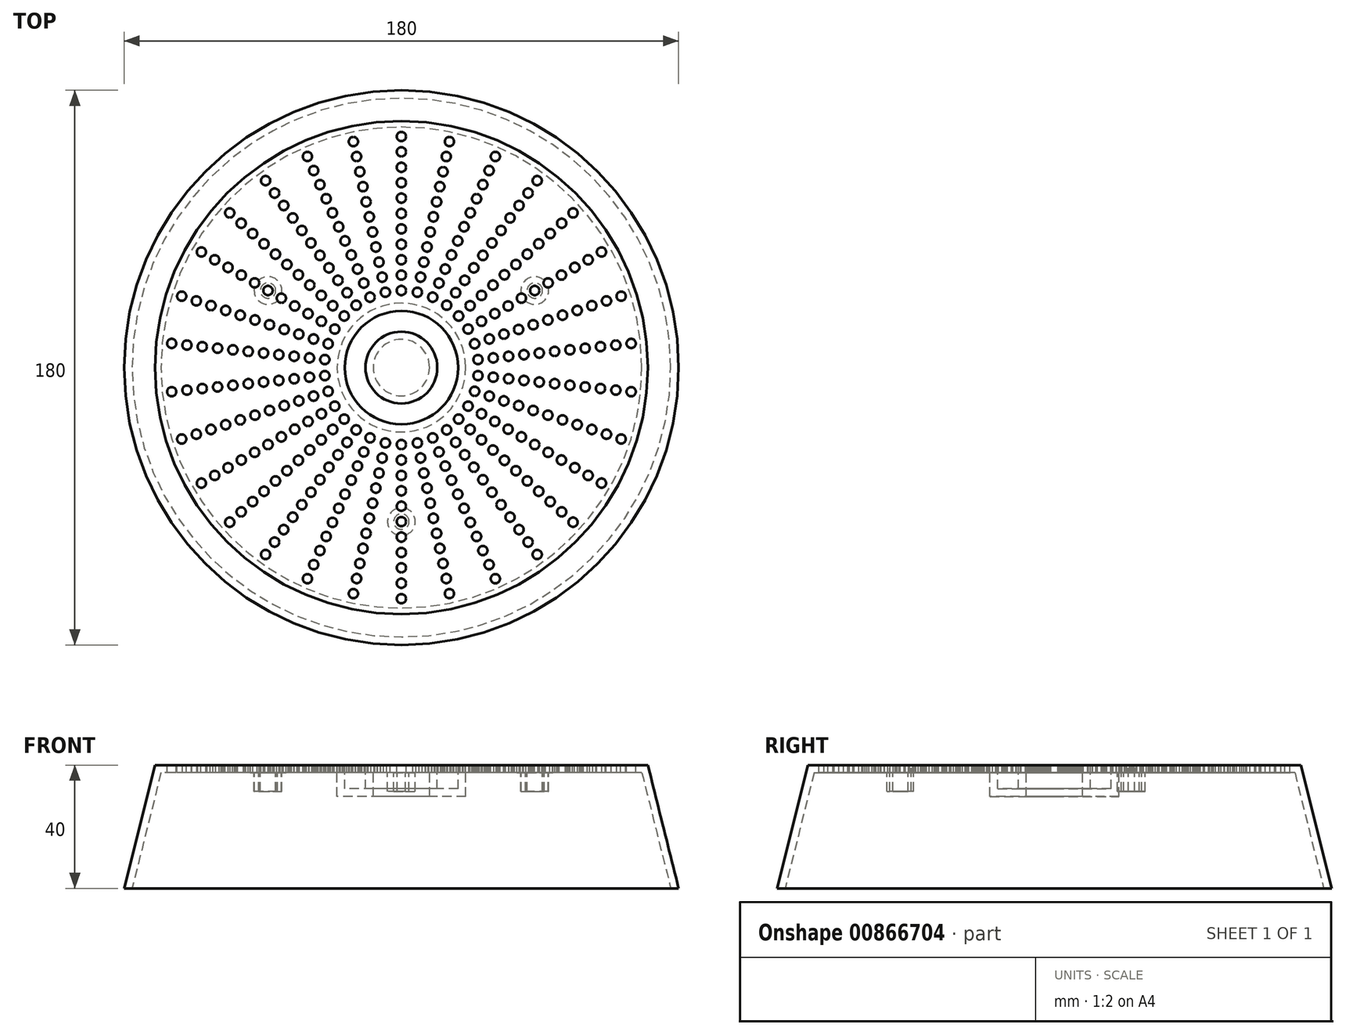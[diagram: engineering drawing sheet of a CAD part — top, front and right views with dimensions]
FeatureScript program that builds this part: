
annotation { "Feature Type Name" : "Feature", "Feature Type Description" : "" }
export const myFeature = defineFeature(function(context is Context, id is Id, definition is map)
    precondition{}
    {
        {
            var Q0;
            Q0=qCreatedBy(makeId("Top.planeOp"),FACE);
            var sketch = newSketch(context, id + "F0", { "sketchPlane" : qUnion([Q0])});
            skCircle(sketch, "E0", {"center": v(0, 0) * mm, "radius": 90 * mm});
            skSolve(sketch);
        }
        {
            var Q0;
            Q0=makeQuery(id+"F0.imprint","IMPRINT",FACE,{"disambiguationData":[TD([[makeQuery(id+"F0.imprint","IMPRINT",EDGE,{"derivedFrom":sQuery(id+"F0.wireOp",EDGE,"E0")}),1.0]])]});
            var Q1;
            Q1=makeQuery(id+"F0.imprint","IMPRINT",FACE,{"disambiguationData":[TD([[makeQuery(id+"F0.imprint","IMPRINT",EDGE,{"derivedFrom":sQuery(id+"F0.wireOp",EDGE,"Ynb0LsxG-EY0P-LQyA-zYZy-US9xmQLmgcTj")}),1.0]])]});
            var Q2;
            Q2=makeQuery(id+"F0.imprint","IMPRINT",FACE,{"disambiguationData":[TD([[makeQuery(id+"F0.imprint","IMPRINT",EDGE,{"derivedFrom":sQuery(id+"F0.wireOp",EDGE,"hYWYR66z-NgrN-YKXc-1CsE-6s0Bsp8cXAIZ")}),1.0]])]});
            extrude(context, id + "F1", {"entities" : qUnion([Q0, Q1, Q2]), "depth" : 40 * mm, "offsetDistance" : 25 * mm});
        }
        {
            var Q0;
            Q0=makeQuery(id+"F1.opExtrude","CAP_FACE",FACE,{"disambiguationData":[OSD([sQuery(id+"F0.wireOp",EDGE,"E0")])],"isStart":false});
            var sketch = newSketch(context, id + "F2", { "sketchPlane" : qUnion([Q0])});
            skCircle(sketch, "E1", {"center": v(0, 0) * mm, "radius": 18.4 * mm});
            skCircle(sketch, "E2", {"center": v(0, 0) * mm, "radius": 11.65 * mm});
            skSolve(sketch);
        }
        {
            var Q0;
            Q0=makeQuery(id+"F2.imprint","IMPRINT",FACE,{"disambiguationData":[TD([[makeQuery(id+"F2.imprint","IMPRINT",EDGE,{"derivedFrom":sQuery(id+"F2.wireOp",EDGE,"E1")}),1.0]])]});
            extrude(context, id + "F3", {"entities" : qUnion([Q0]), "operationType" : NewBodyOperationType.REMOVE, "oppositeDirection" : true, "depth" : 7.7 * mm, "offsetDistance" : 25 * mm});
        }
        {
            var Q0;
            Q0=makeQuery(id+"F1.opExtrude","CAP_EDGE",EDGE,{"disambiguationData":[OSD([sQuery(id+"F0.wireOp",EDGE,"E0")])],"isStart":false});
            chamfer(context, id + "F4", {"entities" : qUnion([Q0]), "chamferType" : ChamferType.TWO_OFFSETS, "width1" : 10 * mm, "oppositeDirection" : false, "width2" : 40 * mm});
        }
        {
            var Q0;
            Q0=makeQuery(id+"F1.opExtrude","CAP_FACE",FACE,{"disambiguationData":[OSD([sQuery(id+"F0.wireOp",EDGE,"E0")])],"isStart":true});
            shell(context, id + "F5", {"entities" : qUnion([Q0]), "thickness" : 2.5 * mm});
        }
        {
            var Q0;
            {var subQ0=sQuery(id+"F0.wireOp",EDGE,"E0");Q0=makeQuery(id+"F5.opShell","OFFSET_FACE",FACE,{"disambiguationData":[OSD([subQ0]),TDD([makeQuery(id+"F3.boolean.opBoolean","SPLIT",FACE,{"disambiguationData":[TD([makeQuery(id+"F1.opExtrude","SWEPT_FACE",FACE,{"disambiguationData":[OSD([subQ0])]})])],"derivedFrom":makeQuery(id+"F1.opExtrude","CAP_FACE",FACE,{"disambiguationData":[OSD([subQ0])],"isStart":false})})])]});}
            var sketch = newSketch(context, id + "F6", { "sketchPlane" : qUnion([Q0])});
            skCircle(sketch, "E3", {"center": v(0, 50) * mm, "radius": 4.5 * mm});
            skCircle(sketch, "E4", {"center": v(0, 50) * mm, "radius": 2.5 * mm});
            skCircle(sketch, "E5.1.0", {"center": v(-43.3, -25) * mm, "radius": 2.5 * mm});
            skCircle(sketch, "E5.1.1", {"center": v(-43.3, -25) * mm, "radius": 4.5 * mm});
            skCircle(sketch, "E5.2.0", {"center": v(43.3, -25) * mm, "radius": 2.5 * mm});
            skCircle(sketch, "E5.2.1", {"center": v(43.3, -25) * mm, "radius": 4.5 * mm});
            skPoint(sketch, "E5.center", {"position": v(0, 0) * mm});
            skSolve(sketch);
        }
        {
            var Q0;
            Q0=makeQuery(id+"F6.imprint","IMPRINT",FACE,{"disambiguationData":[TD([[makeQuery(id+"F6.imprint","IMPRINT",EDGE,{"derivedFrom":sQuery(id+"F6.wireOp",EDGE,"E3")}),1.0]])]});
            var Q1;
            Q1=makeQuery(id+"F6.imprint","IMPRINT",FACE,{"disambiguationData":[TD([[makeQuery(id+"F6.imprint","IMPRINT",EDGE,{"derivedFrom":sQuery(id+"F6.wireOp",EDGE,"E5.2.0")}),-1.0]])]});
            var Q2;
            Q2=makeQuery(id+"F6.imprint","IMPRINT",FACE,{"disambiguationData":[TD([[makeQuery(id+"F6.imprint","IMPRINT",EDGE,{"derivedFrom":sQuery(id+"F6.wireOp",EDGE,"E5.1.0")}),-1.0]])]});
            extrude(context, id + "F7", {"entities" : qUnion([Q0, Q1, Q2]), "operationType" : NewBodyOperationType.ADD, "depth" : 6 * mm, "offsetDistance" : 25 * mm});
        }
        {
            var Q0;
            {var subQ0=sQuery(id+"F0.wireOp",EDGE,"E0");Q0=makeQuery(id+"F3.boolean.opBoolean","SPLIT",FACE,{"disambiguationData":[TD([makeQuery(id+"F1.opExtrude","SWEPT_FACE",FACE,{"disambiguationData":[OSD([subQ0])]})])],"derivedFrom":makeQuery(id+"F1.opExtrude","CAP_FACE",FACE,{"disambiguationData":[OSD([subQ0])],"isStart":false})});}
            var sketch = newSketch(context, id + "F8", { "sketchPlane" : qUnion([Q0])});
            skCircle(sketch, "E6", {"center": v(0, 25) * mm, "radius": 1.5 * mm});
            skCircle(sketch, "E7.0.1.0", {"center": v(0, 30) * mm, "radius": 1.5 * mm});
            skCircle(sketch, "E7.0.2.0", {"center": v(0, 35) * mm, "radius": 1.5 * mm});
            skCircle(sketch, "E7.0.3.0", {"center": v(0, 40) * mm, "radius": 1.5 * mm});
            skCircle(sketch, "E7.0.4.0", {"center": v(0, 45) * mm, "radius": 1.5 * mm});
            skCircle(sketch, "E7.0.5.0", {"center": v(0, 50) * mm, "radius": 1.5 * mm});
            skCircle(sketch, "E7.0.6.0", {"center": v(0, 55) * mm, "radius": 1.5 * mm});
            skCircle(sketch, "E7.0.7.0", {"center": v(0, 60) * mm, "radius": 1.5 * mm});
            skCircle(sketch, "E7.0.8.0", {"center": v(0, 65) * mm, "radius": 1.5 * mm});
            skCircle(sketch, "E7.0.9.0", {"center": v(0, 70) * mm, "radius": 1.5 * mm});
            skCircle(sketch, "E7.0.10.0", {"center": v(0, 75) * mm, "radius": 1.5 * mm});
            skLineSegment(sketch, "E7.direction1", {"start": v(0, 25) * mm, "end": v(6.9, 25) * mm, "construction": true});
            skLineSegment(sketch, "E7.direction2", {"start": v(0, 25) * mm, "end": v(0, 30) * mm, "construction": true});
            skCircle(sketch, "E8.1.0", {"center": v(-10.4, 48.9) * mm, "radius": 1.5 * mm});
            skCircle(sketch, "E8.1.1", {"center": v(-5.2, 24.45) * mm, "radius": 1.5 * mm});
            skCircle(sketch, "E8.1.2", {"center": v(-6.24, 29.34) * mm, "radius": 1.5 * mm});
            skCircle(sketch, "E8.1.3", {"center": v(-7.28, 34.24) * mm, "radius": 1.5 * mm});
            skCircle(sketch, "E8.1.4", {"center": v(-8.32, 39.13) * mm, "radius": 1.5 * mm});
            skCircle(sketch, "E8.1.5", {"center": v(-9.36, 44.02) * mm, "radius": 1.5 * mm});
            skCircle(sketch, "E8.1.6", {"center": v(-11.44, 53.8) * mm, "radius": 1.5 * mm});
            skCircle(sketch, "E8.1.7", {"center": v(-12.47, 58.69) * mm, "radius": 1.5 * mm});
            skCircle(sketch, "E8.1.8", {"center": v(-13.51, 63.58) * mm, "radius": 1.5 * mm});
            skCircle(sketch, "E8.1.9", {"center": v(-14.55, 68.47) * mm, "radius": 1.5 * mm});
            skCircle(sketch, "E8.1.10", {"center": v(-15.6, 73.36) * mm, "radius": 1.5 * mm});
            skCircle(sketch, "E8.2.0", {"center": v(-20.34, 45.68) * mm, "radius": 1.5 * mm});
            skCircle(sketch, "E8.2.1", {"center": v(-10.17, 22.84) * mm, "radius": 1.5 * mm});
            skCircle(sketch, "E8.2.2", {"center": v(-12.2, 27.4) * mm, "radius": 1.5 * mm});
            skCircle(sketch, "E8.2.3", {"center": v(-14.24, 31.97) * mm, "radius": 1.5 * mm});
            skCircle(sketch, "E8.2.4", {"center": v(-16.27, 36.54) * mm, "radius": 1.5 * mm});
            skCircle(sketch, "E8.2.5", {"center": v(-18.3, 41.1) * mm, "radius": 1.5 * mm});
            skCircle(sketch, "E8.2.6", {"center": v(-22.37, 50.25) * mm, "radius": 1.5 * mm});
            skCircle(sketch, "E8.2.7", {"center": v(-24.4, 54.81) * mm, "radius": 1.5 * mm});
            skCircle(sketch, "E8.2.8", {"center": v(-26.44, 59.38) * mm, "radius": 1.5 * mm});
            skCircle(sketch, "E8.2.9", {"center": v(-28.47, 63.95) * mm, "radius": 1.5 * mm});
            skCircle(sketch, "E8.2.10", {"center": v(-30.5, 68.52) * mm, "radius": 1.5 * mm});
            skCircle(sketch, "E8.3.0", {"center": v(-29.39, 40.45) * mm, "radius": 1.5 * mm});
            skCircle(sketch, "E8.3.1", {"center": v(-14.7, 20.23) * mm, "radius": 1.5 * mm});
            skCircle(sketch, "E8.3.2", {"center": v(-17.63, 24.27) * mm, "radius": 1.5 * mm});
            skCircle(sketch, "E8.3.3", {"center": v(-20.57, 28.32) * mm, "radius": 1.5 * mm});
            skCircle(sketch, "E8.3.4", {"center": v(-23.51, 32.36) * mm, "radius": 1.5 * mm});
            skCircle(sketch, "E8.3.5", {"center": v(-26.45, 36.4) * mm, "radius": 1.5 * mm});
            skCircle(sketch, "E8.3.6", {"center": v(-32.33, 44.5) * mm, "radius": 1.5 * mm});
            skCircle(sketch, "E8.3.7", {"center": v(-35.27, 48.54) * mm, "radius": 1.5 * mm});
            skCircle(sketch, "E8.3.8", {"center": v(-38.2, 52.59) * mm, "radius": 1.5 * mm});
            skCircle(sketch, "E8.3.9", {"center": v(-41.14, 56.63) * mm, "radius": 1.5 * mm});
            skCircle(sketch, "E8.3.10", {"center": v(-44.08, 60.68) * mm, "radius": 1.5 * mm});
            skCircle(sketch, "E8.4.0", {"center": v(-37.16, 33.46) * mm, "radius": 1.5 * mm});
            skCircle(sketch, "E8.4.1", {"center": v(-18.58, 16.73) * mm, "radius": 1.5 * mm});
            skCircle(sketch, "E8.4.2", {"center": v(-22.3, 20.07) * mm, "radius": 1.5 * mm});
            skCircle(sketch, "E8.4.3", {"center": v(-26.01, 23.42) * mm, "radius": 1.5 * mm});
            skCircle(sketch, "E8.4.4", {"center": v(-29.73, 26.77) * mm, "radius": 1.5 * mm});
            skCircle(sketch, "E8.4.5", {"center": v(-33.44, 30.11) * mm, "radius": 1.5 * mm});
            skCircle(sketch, "E8.4.6", {"center": v(-40.87, 36.8) * mm, "radius": 1.5 * mm});
            skCircle(sketch, "E8.4.7", {"center": v(-44.59, 40.15) * mm, "radius": 1.5 * mm});
            skCircle(sketch, "E8.4.8", {"center": v(-48.3, 43.5) * mm, "radius": 1.5 * mm});
            skCircle(sketch, "E8.4.9", {"center": v(-52.02, 46.84) * mm, "radius": 1.5 * mm});
            skCircle(sketch, "E8.4.10", {"center": v(-55.74, 50.18) * mm, "radius": 1.5 * mm});
            skCircle(sketch, "E8.5.0", {"center": v(-43.3, 25) * mm, "radius": 1.5 * mm});
            skCircle(sketch, "E8.5.1", {"center": v(-21.65, 12.5) * mm, "radius": 1.5 * mm});
            skCircle(sketch, "E8.5.2", {"center": v(-25.98, 15) * mm, "radius": 1.5 * mm});
            skCircle(sketch, "E8.5.3", {"center": v(-30.31, 17.5) * mm, "radius": 1.5 * mm});
            skCircle(sketch, "E8.5.4", {"center": v(-34.64, 20) * mm, "radius": 1.5 * mm});
            skCircle(sketch, "E8.5.5", {"center": v(-38.97, 22.5) * mm, "radius": 1.5 * mm});
            skCircle(sketch, "E8.5.6", {"center": v(-47.63, 27.5) * mm, "radius": 1.5 * mm});
            skCircle(sketch, "E8.5.7", {"center": v(-51.96, 30) * mm, "radius": 1.5 * mm});
            skCircle(sketch, "E8.5.8", {"center": v(-56.3, 32.5) * mm, "radius": 1.5 * mm});
            skCircle(sketch, "E8.5.9", {"center": v(-60.62, 35) * mm, "radius": 1.5 * mm});
            skCircle(sketch, "E8.5.10", {"center": v(-64.95, 37.5) * mm, "radius": 1.5 * mm});
            skCircle(sketch, "E8.6.0", {"center": v(-47.55, 15.45) * mm, "radius": 1.5 * mm});
            skCircle(sketch, "E8.6.1", {"center": v(-23.78, 7.73) * mm, "radius": 1.5 * mm});
            skCircle(sketch, "E8.6.2", {"center": v(-28.53, 9.27) * mm, "radius": 1.5 * mm});
            skCircle(sketch, "E8.6.3", {"center": v(-33.29, 10.82) * mm, "radius": 1.5 * mm});
            skCircle(sketch, "E8.6.4", {"center": v(-38.04, 12.36) * mm, "radius": 1.5 * mm});
            skCircle(sketch, "E8.6.5", {"center": v(-42.8, 13.9) * mm, "radius": 1.5 * mm});
            skCircle(sketch, "E8.6.6", {"center": v(-52.3, 17) * mm, "radius": 1.5 * mm});
            skCircle(sketch, "E8.6.7", {"center": v(-57.06, 18.54) * mm, "radius": 1.5 * mm});
            skCircle(sketch, "E8.6.8", {"center": v(-61.82, 20.09) * mm, "radius": 1.5 * mm});
            skCircle(sketch, "E8.6.9", {"center": v(-66.57, 21.63) * mm, "radius": 1.5 * mm});
            skCircle(sketch, "E8.6.10", {"center": v(-71.33, 23.18) * mm, "radius": 1.5 * mm});
            skCircle(sketch, "E8.7.0", {"center": v(-49.73, 5.23) * mm, "radius": 1.5 * mm});
            skCircle(sketch, "E8.7.1", {"center": v(-24.86, 2.61) * mm, "radius": 1.5 * mm});
            skCircle(sketch, "E8.7.2", {"center": v(-29.84, 3.14) * mm, "radius": 1.5 * mm});
            skCircle(sketch, "E8.7.3", {"center": v(-34.8, 3.66) * mm, "radius": 1.5 * mm});
            skCircle(sketch, "E8.7.4", {"center": v(-39.78, 4.18) * mm, "radius": 1.5 * mm});
            skCircle(sketch, "E8.7.5", {"center": v(-44.75, 4.7) * mm, "radius": 1.5 * mm});
            skCircle(sketch, "E8.7.6", {"center": v(-54.7, 5.75) * mm, "radius": 1.5 * mm});
            skCircle(sketch, "E8.7.7", {"center": v(-59.67, 6.27) * mm, "radius": 1.5 * mm});
            skCircle(sketch, "E8.7.8", {"center": v(-64.64, 6.8) * mm, "radius": 1.5 * mm});
            skCircle(sketch, "E8.7.9", {"center": v(-69.62, 7.32) * mm, "radius": 1.5 * mm});
            skCircle(sketch, "E8.7.10", {"center": v(-74.59, 7.84) * mm, "radius": 1.5 * mm});
            skCircle(sketch, "E8.8.0", {"center": v(-49.73, -5.23) * mm, "radius": 1.5 * mm});
            skCircle(sketch, "E8.8.1", {"center": v(-24.86, -2.61) * mm, "radius": 1.5 * mm});
            skCircle(sketch, "E8.8.2", {"center": v(-29.84, -3.14) * mm, "radius": 1.5 * mm});
            skCircle(sketch, "E8.8.3", {"center": v(-34.8, -3.66) * mm, "radius": 1.5 * mm});
            skCircle(sketch, "E8.8.4", {"center": v(-39.78, -4.18) * mm, "radius": 1.5 * mm});
            skCircle(sketch, "E8.8.5", {"center": v(-44.75, -4.7) * mm, "radius": 1.5 * mm});
            skCircle(sketch, "E8.8.6", {"center": v(-54.7, -5.75) * mm, "radius": 1.5 * mm});
            skCircle(sketch, "E8.8.7", {"center": v(-59.67, -6.27) * mm, "radius": 1.5 * mm});
            skCircle(sketch, "E8.8.8", {"center": v(-64.64, -6.8) * mm, "radius": 1.5 * mm});
            skCircle(sketch, "E8.8.9", {"center": v(-69.62, -7.32) * mm, "radius": 1.5 * mm});
            skCircle(sketch, "E8.8.10", {"center": v(-74.59, -7.84) * mm, "radius": 1.5 * mm});
            skCircle(sketch, "E8.9.0", {"center": v(-47.55, -15.45) * mm, "radius": 1.5 * mm});
            skCircle(sketch, "E8.9.1", {"center": v(-23.78, -7.73) * mm, "radius": 1.5 * mm});
            skCircle(sketch, "E8.9.2", {"center": v(-28.53, -9.27) * mm, "radius": 1.5 * mm});
            skCircle(sketch, "E8.9.3", {"center": v(-33.29, -10.82) * mm, "radius": 1.5 * mm});
            skCircle(sketch, "E8.9.4", {"center": v(-38.04, -12.36) * mm, "radius": 1.5 * mm});
            skCircle(sketch, "E8.9.5", {"center": v(-42.8, -13.9) * mm, "radius": 1.5 * mm});
            skCircle(sketch, "E8.9.6", {"center": v(-52.3, -17) * mm, "radius": 1.5 * mm});
            skCircle(sketch, "E8.9.7", {"center": v(-57.06, -18.54) * mm, "radius": 1.5 * mm});
            skCircle(sketch, "E8.9.8", {"center": v(-61.82, -20.09) * mm, "radius": 1.5 * mm});
            skCircle(sketch, "E8.9.9", {"center": v(-66.57, -21.63) * mm, "radius": 1.5 * mm});
            skCircle(sketch, "E8.9.10", {"center": v(-71.33, -23.18) * mm, "radius": 1.5 * mm});
            skCircle(sketch, "E8.10.0", {"center": v(-43.3, -25) * mm, "radius": 1.5 * mm});
            skCircle(sketch, "E8.10.1", {"center": v(-21.65, -12.5) * mm, "radius": 1.5 * mm});
            skCircle(sketch, "E8.10.2", {"center": v(-25.98, -15) * mm, "radius": 1.5 * mm});
            skCircle(sketch, "E8.10.3", {"center": v(-30.31, -17.5) * mm, "radius": 1.5 * mm});
            skCircle(sketch, "E8.10.4", {"center": v(-34.64, -20) * mm, "radius": 1.5 * mm});
            skCircle(sketch, "E8.10.5", {"center": v(-38.97, -22.5) * mm, "radius": 1.5 * mm});
            skCircle(sketch, "E8.10.6", {"center": v(-47.63, -27.5) * mm, "radius": 1.5 * mm});
            skCircle(sketch, "E8.10.7", {"center": v(-51.96, -30) * mm, "radius": 1.5 * mm});
            skCircle(sketch, "E8.10.8", {"center": v(-56.3, -32.5) * mm, "radius": 1.5 * mm});
            skCircle(sketch, "E8.10.9", {"center": v(-60.62, -35) * mm, "radius": 1.5 * mm});
            skCircle(sketch, "E8.10.10", {"center": v(-64.95, -37.5) * mm, "radius": 1.5 * mm});
            skCircle(sketch, "E8.11.0", {"center": v(-37.16, -33.46) * mm, "radius": 1.5 * mm});
            skCircle(sketch, "E8.11.1", {"center": v(-18.58, -16.73) * mm, "radius": 1.5 * mm});
            skCircle(sketch, "E8.11.2", {"center": v(-22.3, -20.07) * mm, "radius": 1.5 * mm});
            skCircle(sketch, "E8.11.3", {"center": v(-26.01, -23.42) * mm, "radius": 1.5 * mm});
            skCircle(sketch, "E8.11.4", {"center": v(-29.73, -26.77) * mm, "radius": 1.5 * mm});
            skCircle(sketch, "E8.11.5", {"center": v(-33.44, -30.11) * mm, "radius": 1.5 * mm});
            skCircle(sketch, "E8.11.6", {"center": v(-40.87, -36.8) * mm, "radius": 1.5 * mm});
            skCircle(sketch, "E8.11.7", {"center": v(-44.59, -40.15) * mm, "radius": 1.5 * mm});
            skCircle(sketch, "E8.11.8", {"center": v(-48.3, -43.5) * mm, "radius": 1.5 * mm});
            skCircle(sketch, "E8.11.9", {"center": v(-52.02, -46.84) * mm, "radius": 1.5 * mm});
            skCircle(sketch, "E8.11.10", {"center": v(-55.74, -50.18) * mm, "radius": 1.5 * mm});
            skCircle(sketch, "E8.12.0", {"center": v(-29.39, -40.45) * mm, "radius": 1.5 * mm});
            skCircle(sketch, "E8.12.1", {"center": v(-14.7, -20.23) * mm, "radius": 1.5 * mm});
            skCircle(sketch, "E8.12.2", {"center": v(-17.63, -24.27) * mm, "radius": 1.5 * mm});
            skCircle(sketch, "E8.12.3", {"center": v(-20.57, -28.32) * mm, "radius": 1.5 * mm});
            skCircle(sketch, "E8.12.4", {"center": v(-23.51, -32.36) * mm, "radius": 1.5 * mm});
            skCircle(sketch, "E8.12.5", {"center": v(-26.45, -36.4) * mm, "radius": 1.5 * mm});
            skCircle(sketch, "E8.12.6", {"center": v(-32.33, -44.5) * mm, "radius": 1.5 * mm});
            skCircle(sketch, "E8.12.7", {"center": v(-35.27, -48.54) * mm, "radius": 1.5 * mm});
            skCircle(sketch, "E8.12.8", {"center": v(-38.2, -52.59) * mm, "radius": 1.5 * mm});
            skCircle(sketch, "E8.12.9", {"center": v(-41.14, -56.63) * mm, "radius": 1.5 * mm});
            skCircle(sketch, "E8.12.10", {"center": v(-44.08, -60.68) * mm, "radius": 1.5 * mm});
            skCircle(sketch, "E8.13.0", {"center": v(-20.34, -45.68) * mm, "radius": 1.5 * mm});
            skCircle(sketch, "E8.13.1", {"center": v(-10.17, -22.84) * mm, "radius": 1.5 * mm});
            skCircle(sketch, "E8.13.2", {"center": v(-12.2, -27.4) * mm, "radius": 1.5 * mm});
            skCircle(sketch, "E8.13.3", {"center": v(-14.24, -31.97) * mm, "radius": 1.5 * mm});
            skCircle(sketch, "E8.13.4", {"center": v(-16.27, -36.54) * mm, "radius": 1.5 * mm});
            skCircle(sketch, "E8.13.5", {"center": v(-18.3, -41.1) * mm, "radius": 1.5 * mm});
            skCircle(sketch, "E8.13.6", {"center": v(-22.37, -50.25) * mm, "radius": 1.5 * mm});
            skCircle(sketch, "E8.13.7", {"center": v(-24.4, -54.81) * mm, "radius": 1.5 * mm});
            skCircle(sketch, "E8.13.8", {"center": v(-26.44, -59.38) * mm, "radius": 1.5 * mm});
            skCircle(sketch, "E8.13.9", {"center": v(-28.47, -63.95) * mm, "radius": 1.5 * mm});
            skCircle(sketch, "E8.13.10", {"center": v(-30.5, -68.52) * mm, "radius": 1.5 * mm});
            skCircle(sketch, "E8.14.0", {"center": v(-10.4, -48.9) * mm, "radius": 1.5 * mm});
            skCircle(sketch, "E8.14.1", {"center": v(-5.2, -24.45) * mm, "radius": 1.5 * mm});
            skCircle(sketch, "E8.14.2", {"center": v(-6.24, -29.34) * mm, "radius": 1.5 * mm});
            skCircle(sketch, "E8.14.3", {"center": v(-7.28, -34.24) * mm, "radius": 1.5 * mm});
            skCircle(sketch, "E8.14.4", {"center": v(-8.32, -39.13) * mm, "radius": 1.5 * mm});
            skCircle(sketch, "E8.14.5", {"center": v(-9.36, -44.02) * mm, "radius": 1.5 * mm});
            skCircle(sketch, "E8.14.6", {"center": v(-11.44, -53.8) * mm, "radius": 1.5 * mm});
            skCircle(sketch, "E8.14.7", {"center": v(-12.47, -58.69) * mm, "radius": 1.5 * mm});
            skCircle(sketch, "E8.14.8", {"center": v(-13.51, -63.58) * mm, "radius": 1.5 * mm});
            skCircle(sketch, "E8.14.9", {"center": v(-14.55, -68.47) * mm, "radius": 1.5 * mm});
            skCircle(sketch, "E8.14.10", {"center": v(-15.6, -73.36) * mm, "radius": 1.5 * mm});
            skCircle(sketch, "E8.15.0", {"center": v(0, -50) * mm, "radius": 1.5 * mm});
            skCircle(sketch, "E8.15.1", {"center": v(0, -25) * mm, "radius": 1.5 * mm});
            skCircle(sketch, "E8.15.2", {"center": v(0, -30) * mm, "radius": 1.5 * mm});
            skCircle(sketch, "E8.15.3", {"center": v(0, -35) * mm, "radius": 1.5 * mm});
            skCircle(sketch, "E8.15.4", {"center": v(0, -40) * mm, "radius": 1.5 * mm});
            skCircle(sketch, "E8.15.5", {"center": v(0, -45) * mm, "radius": 1.5 * mm});
            skCircle(sketch, "E8.15.6", {"center": v(0, -55) * mm, "radius": 1.5 * mm});
            skCircle(sketch, "E8.15.7", {"center": v(0, -60) * mm, "radius": 1.5 * mm});
            skCircle(sketch, "E8.15.8", {"center": v(0, -65) * mm, "radius": 1.5 * mm});
            skCircle(sketch, "E8.15.9", {"center": v(0, -70) * mm, "radius": 1.5 * mm});
            skCircle(sketch, "E8.15.10", {"center": v(0, -75) * mm, "radius": 1.5 * mm});
            skCircle(sketch, "E8.16.0", {"center": v(10.4, -48.9) * mm, "radius": 1.5 * mm});
            skCircle(sketch, "E8.16.1", {"center": v(5.2, -24.45) * mm, "radius": 1.5 * mm});
            skCircle(sketch, "E8.16.2", {"center": v(6.24, -29.34) * mm, "radius": 1.5 * mm});
            skCircle(sketch, "E8.16.3", {"center": v(7.28, -34.24) * mm, "radius": 1.5 * mm});
            skCircle(sketch, "E8.16.4", {"center": v(8.32, -39.13) * mm, "radius": 1.5 * mm});
            skCircle(sketch, "E8.16.5", {"center": v(9.36, -44.02) * mm, "radius": 1.5 * mm});
            skCircle(sketch, "E8.16.6", {"center": v(11.44, -53.8) * mm, "radius": 1.5 * mm});
            skCircle(sketch, "E8.16.7", {"center": v(12.47, -58.69) * mm, "radius": 1.5 * mm});
            skCircle(sketch, "E8.16.8", {"center": v(13.51, -63.58) * mm, "radius": 1.5 * mm});
            skCircle(sketch, "E8.16.9", {"center": v(14.55, -68.47) * mm, "radius": 1.5 * mm});
            skCircle(sketch, "E8.16.10", {"center": v(15.6, -73.36) * mm, "radius": 1.5 * mm});
            skCircle(sketch, "E8.17.0", {"center": v(20.34, -45.68) * mm, "radius": 1.5 * mm});
            skCircle(sketch, "E8.17.1", {"center": v(10.17, -22.84) * mm, "radius": 1.5 * mm});
            skCircle(sketch, "E8.17.2", {"center": v(12.2, -27.4) * mm, "radius": 1.5 * mm});
            skCircle(sketch, "E8.17.3", {"center": v(14.24, -31.97) * mm, "radius": 1.5 * mm});
            skCircle(sketch, "E8.17.4", {"center": v(16.27, -36.54) * mm, "radius": 1.5 * mm});
            skCircle(sketch, "E8.17.5", {"center": v(18.3, -41.1) * mm, "radius": 1.5 * mm});
            skCircle(sketch, "E8.17.6", {"center": v(22.37, -50.25) * mm, "radius": 1.5 * mm});
            skCircle(sketch, "E8.17.7", {"center": v(24.4, -54.81) * mm, "radius": 1.5 * mm});
            skCircle(sketch, "E8.17.8", {"center": v(26.44, -59.38) * mm, "radius": 1.5 * mm});
            skCircle(sketch, "E8.17.9", {"center": v(28.47, -63.95) * mm, "radius": 1.5 * mm});
            skCircle(sketch, "E8.17.10", {"center": v(30.5, -68.52) * mm, "radius": 1.5 * mm});
            skCircle(sketch, "E8.18.0", {"center": v(29.39, -40.45) * mm, "radius": 1.5 * mm});
            skCircle(sketch, "E8.18.1", {"center": v(14.7, -20.23) * mm, "radius": 1.5 * mm});
            skCircle(sketch, "E8.18.2", {"center": v(17.63, -24.27) * mm, "radius": 1.5 * mm});
            skCircle(sketch, "E8.18.3", {"center": v(20.57, -28.32) * mm, "radius": 1.5 * mm});
            skCircle(sketch, "E8.18.4", {"center": v(23.51, -32.36) * mm, "radius": 1.5 * mm});
            skCircle(sketch, "E8.18.5", {"center": v(26.45, -36.4) * mm, "radius": 1.5 * mm});
            skCircle(sketch, "E8.18.6", {"center": v(32.33, -44.5) * mm, "radius": 1.5 * mm});
            skCircle(sketch, "E8.18.7", {"center": v(35.27, -48.54) * mm, "radius": 1.5 * mm});
            skCircle(sketch, "E8.18.8", {"center": v(38.2, -52.59) * mm, "radius": 1.5 * mm});
            skCircle(sketch, "E8.18.9", {"center": v(41.14, -56.63) * mm, "radius": 1.5 * mm});
            skCircle(sketch, "E8.18.10", {"center": v(44.08, -60.68) * mm, "radius": 1.5 * mm});
            skCircle(sketch, "E8.19.0", {"center": v(37.16, -33.46) * mm, "radius": 1.5 * mm});
            skCircle(sketch, "E8.19.1", {"center": v(18.58, -16.73) * mm, "radius": 1.5 * mm});
            skCircle(sketch, "E8.19.2", {"center": v(22.3, -20.07) * mm, "radius": 1.5 * mm});
            skCircle(sketch, "E8.19.3", {"center": v(26.01, -23.42) * mm, "radius": 1.5 * mm});
            skCircle(sketch, "E8.19.4", {"center": v(29.73, -26.77) * mm, "radius": 1.5 * mm});
            skCircle(sketch, "E8.19.5", {"center": v(33.44, -30.11) * mm, "radius": 1.5 * mm});
            skCircle(sketch, "E8.19.6", {"center": v(40.87, -36.8) * mm, "radius": 1.5 * mm});
            skCircle(sketch, "E8.19.7", {"center": v(44.59, -40.15) * mm, "radius": 1.5 * mm});
            skCircle(sketch, "E8.19.8", {"center": v(48.3, -43.5) * mm, "radius": 1.5 * mm});
            skCircle(sketch, "E8.19.9", {"center": v(52.02, -46.84) * mm, "radius": 1.5 * mm});
            skCircle(sketch, "E8.19.10", {"center": v(55.74, -50.18) * mm, "radius": 1.5 * mm});
            skCircle(sketch, "E8.20.0", {"center": v(43.3, -25) * mm, "radius": 1.5 * mm});
            skCircle(sketch, "E8.20.1", {"center": v(21.65, -12.5) * mm, "radius": 1.5 * mm});
            skCircle(sketch, "E8.20.2", {"center": v(25.98, -15) * mm, "radius": 1.5 * mm});
            skCircle(sketch, "E8.20.3", {"center": v(30.31, -17.5) * mm, "radius": 1.5 * mm});
            skCircle(sketch, "E8.20.4", {"center": v(34.64, -20) * mm, "radius": 1.5 * mm});
            skCircle(sketch, "E8.20.5", {"center": v(38.97, -22.5) * mm, "radius": 1.5 * mm});
            skCircle(sketch, "E8.20.6", {"center": v(47.63, -27.5) * mm, "radius": 1.5 * mm});
            skCircle(sketch, "E8.20.7", {"center": v(51.96, -30) * mm, "radius": 1.5 * mm});
            skCircle(sketch, "E8.20.8", {"center": v(56.3, -32.5) * mm, "radius": 1.5 * mm});
            skCircle(sketch, "E8.20.9", {"center": v(60.62, -35) * mm, "radius": 1.5 * mm});
            skCircle(sketch, "E8.20.10", {"center": v(64.95, -37.5) * mm, "radius": 1.5 * mm});
            skCircle(sketch, "E8.21.0", {"center": v(47.55, -15.45) * mm, "radius": 1.5 * mm});
            skCircle(sketch, "E8.21.1", {"center": v(23.78, -7.73) * mm, "radius": 1.5 * mm});
            skCircle(sketch, "E8.21.2", {"center": v(28.53, -9.27) * mm, "radius": 1.5 * mm});
            skCircle(sketch, "E8.21.3", {"center": v(33.29, -10.82) * mm, "radius": 1.5 * mm});
            skCircle(sketch, "E8.21.4", {"center": v(38.04, -12.36) * mm, "radius": 1.5 * mm});
            skCircle(sketch, "E8.21.5", {"center": v(42.8, -13.9) * mm, "radius": 1.5 * mm});
            skCircle(sketch, "E8.21.6", {"center": v(52.3, -17) * mm, "radius": 1.5 * mm});
            skCircle(sketch, "E8.21.7", {"center": v(57.06, -18.54) * mm, "radius": 1.5 * mm});
            skCircle(sketch, "E8.21.8", {"center": v(61.82, -20.09) * mm, "radius": 1.5 * mm});
            skCircle(sketch, "E8.21.9", {"center": v(66.57, -21.63) * mm, "radius": 1.5 * mm});
            skCircle(sketch, "E8.21.10", {"center": v(71.33, -23.18) * mm, "radius": 1.5 * mm});
            skCircle(sketch, "E8.22.0", {"center": v(49.73, -5.23) * mm, "radius": 1.5 * mm});
            skCircle(sketch, "E8.22.1", {"center": v(24.86, -2.61) * mm, "radius": 1.5 * mm});
            skCircle(sketch, "E8.22.2", {"center": v(29.84, -3.14) * mm, "radius": 1.5 * mm});
            skCircle(sketch, "E8.22.3", {"center": v(34.8, -3.66) * mm, "radius": 1.5 * mm});
            skCircle(sketch, "E8.22.4", {"center": v(39.78, -4.18) * mm, "radius": 1.5 * mm});
            skCircle(sketch, "E8.22.5", {"center": v(44.75, -4.7) * mm, "radius": 1.5 * mm});
            skCircle(sketch, "E8.22.6", {"center": v(54.7, -5.75) * mm, "radius": 1.5 * mm});
            skCircle(sketch, "E8.22.7", {"center": v(59.67, -6.27) * mm, "radius": 1.5 * mm});
            skCircle(sketch, "E8.22.8", {"center": v(64.64, -6.8) * mm, "radius": 1.5 * mm});
            skCircle(sketch, "E8.22.9", {"center": v(69.62, -7.32) * mm, "radius": 1.5 * mm});
            skCircle(sketch, "E8.22.10", {"center": v(74.59, -7.84) * mm, "radius": 1.5 * mm});
            skCircle(sketch, "E8.23.0", {"center": v(49.73, 5.23) * mm, "radius": 1.5 * mm});
            skCircle(sketch, "E8.23.1", {"center": v(24.86, 2.61) * mm, "radius": 1.5 * mm});
            skCircle(sketch, "E8.23.2", {"center": v(29.84, 3.14) * mm, "radius": 1.5 * mm});
            skCircle(sketch, "E8.23.3", {"center": v(34.8, 3.66) * mm, "radius": 1.5 * mm});
            skCircle(sketch, "E8.23.4", {"center": v(39.78, 4.18) * mm, "radius": 1.5 * mm});
            skCircle(sketch, "E8.23.5", {"center": v(44.75, 4.7) * mm, "radius": 1.5 * mm});
            skCircle(sketch, "E8.23.6", {"center": v(54.7, 5.75) * mm, "radius": 1.5 * mm});
            skCircle(sketch, "E8.23.7", {"center": v(59.67, 6.27) * mm, "radius": 1.5 * mm});
            skCircle(sketch, "E8.23.8", {"center": v(64.64, 6.8) * mm, "radius": 1.5 * mm});
            skCircle(sketch, "E8.23.9", {"center": v(69.62, 7.32) * mm, "radius": 1.5 * mm});
            skCircle(sketch, "E8.23.10", {"center": v(74.59, 7.84) * mm, "radius": 1.5 * mm});
            skCircle(sketch, "E8.24.0", {"center": v(47.55, 15.45) * mm, "radius": 1.5 * mm});
            skCircle(sketch, "E8.24.1", {"center": v(23.78, 7.73) * mm, "radius": 1.5 * mm});
            skCircle(sketch, "E8.24.2", {"center": v(28.53, 9.27) * mm, "radius": 1.5 * mm});
            skCircle(sketch, "E8.24.3", {"center": v(33.29, 10.82) * mm, "radius": 1.5 * mm});
            skCircle(sketch, "E8.24.4", {"center": v(38.04, 12.36) * mm, "radius": 1.5 * mm});
            skCircle(sketch, "E8.24.5", {"center": v(42.8, 13.9) * mm, "radius": 1.5 * mm});
            skCircle(sketch, "E8.24.6", {"center": v(52.3, 17) * mm, "radius": 1.5 * mm});
            skCircle(sketch, "E8.24.7", {"center": v(57.06, 18.54) * mm, "radius": 1.5 * mm});
            skCircle(sketch, "E8.24.8", {"center": v(61.82, 20.09) * mm, "radius": 1.5 * mm});
            skCircle(sketch, "E8.24.9", {"center": v(66.57, 21.63) * mm, "radius": 1.5 * mm});
            skCircle(sketch, "E8.24.10", {"center": v(71.33, 23.18) * mm, "radius": 1.5 * mm});
            skCircle(sketch, "E8.25.0", {"center": v(43.3, 25) * mm, "radius": 1.5 * mm});
            skCircle(sketch, "E8.25.1", {"center": v(21.65, 12.5) * mm, "radius": 1.5 * mm});
            skCircle(sketch, "E8.25.2", {"center": v(25.98, 15) * mm, "radius": 1.5 * mm});
            skCircle(sketch, "E8.25.3", {"center": v(30.31, 17.5) * mm, "radius": 1.5 * mm});
            skCircle(sketch, "E8.25.4", {"center": v(34.64, 20) * mm, "radius": 1.5 * mm});
            skCircle(sketch, "E8.25.5", {"center": v(38.97, 22.5) * mm, "radius": 1.5 * mm});
            skCircle(sketch, "E8.25.6", {"center": v(47.63, 27.5) * mm, "radius": 1.5 * mm});
            skCircle(sketch, "E8.25.7", {"center": v(51.96, 30) * mm, "radius": 1.5 * mm});
            skCircle(sketch, "E8.25.8", {"center": v(56.3, 32.5) * mm, "radius": 1.5 * mm});
            skCircle(sketch, "E8.25.9", {"center": v(60.62, 35) * mm, "radius": 1.5 * mm});
            skCircle(sketch, "E8.25.10", {"center": v(64.95, 37.5) * mm, "radius": 1.5 * mm});
            skCircle(sketch, "E8.26.0", {"center": v(37.16, 33.46) * mm, "radius": 1.5 * mm});
            skCircle(sketch, "E8.26.1", {"center": v(18.58, 16.73) * mm, "radius": 1.5 * mm});
            skCircle(sketch, "E8.26.2", {"center": v(22.3, 20.07) * mm, "radius": 1.5 * mm});
            skCircle(sketch, "E8.26.3", {"center": v(26.01, 23.42) * mm, "radius": 1.5 * mm});
            skCircle(sketch, "E8.26.4", {"center": v(29.73, 26.77) * mm, "radius": 1.5 * mm});
            skCircle(sketch, "E8.26.5", {"center": v(33.44, 30.11) * mm, "radius": 1.5 * mm});
            skCircle(sketch, "E8.26.6", {"center": v(40.87, 36.8) * mm, "radius": 1.5 * mm});
            skCircle(sketch, "E8.26.7", {"center": v(44.59, 40.15) * mm, "radius": 1.5 * mm});
            skCircle(sketch, "E8.26.8", {"center": v(48.3, 43.5) * mm, "radius": 1.5 * mm});
            skCircle(sketch, "E8.26.9", {"center": v(52.02, 46.84) * mm, "radius": 1.5 * mm});
            skCircle(sketch, "E8.26.10", {"center": v(55.74, 50.18) * mm, "radius": 1.5 * mm});
            skCircle(sketch, "E8.27.0", {"center": v(29.39, 40.45) * mm, "radius": 1.5 * mm});
            skCircle(sketch, "E8.27.1", {"center": v(14.7, 20.23) * mm, "radius": 1.5 * mm});
            skCircle(sketch, "E8.27.2", {"center": v(17.63, 24.27) * mm, "radius": 1.5 * mm});
            skCircle(sketch, "E8.27.3", {"center": v(20.57, 28.32) * mm, "radius": 1.5 * mm});
            skCircle(sketch, "E8.27.4", {"center": v(23.51, 32.36) * mm, "radius": 1.5 * mm});
            skCircle(sketch, "E8.27.5", {"center": v(26.45, 36.4) * mm, "radius": 1.5 * mm});
            skCircle(sketch, "E8.27.6", {"center": v(32.33, 44.5) * mm, "radius": 1.5 * mm});
            skCircle(sketch, "E8.27.7", {"center": v(35.27, 48.54) * mm, "radius": 1.5 * mm});
            skCircle(sketch, "E8.27.8", {"center": v(38.2, 52.59) * mm, "radius": 1.5 * mm});
            skCircle(sketch, "E8.27.9", {"center": v(41.14, 56.63) * mm, "radius": 1.5 * mm});
            skCircle(sketch, "E8.27.10", {"center": v(44.08, 60.68) * mm, "radius": 1.5 * mm});
            skCircle(sketch, "E8.28.0", {"center": v(20.34, 45.68) * mm, "radius": 1.5 * mm});
            skCircle(sketch, "E8.28.1", {"center": v(10.17, 22.84) * mm, "radius": 1.5 * mm});
            skCircle(sketch, "E8.28.2", {"center": v(12.2, 27.4) * mm, "radius": 1.5 * mm});
            skCircle(sketch, "E8.28.3", {"center": v(14.24, 31.97) * mm, "radius": 1.5 * mm});
            skCircle(sketch, "E8.28.4", {"center": v(16.27, 36.54) * mm, "radius": 1.5 * mm});
            skCircle(sketch, "E8.28.5", {"center": v(18.3, 41.1) * mm, "radius": 1.5 * mm});
            skCircle(sketch, "E8.28.6", {"center": v(22.37, 50.25) * mm, "radius": 1.5 * mm});
            skCircle(sketch, "E8.28.7", {"center": v(24.4, 54.81) * mm, "radius": 1.5 * mm});
            skCircle(sketch, "E8.28.8", {"center": v(26.44, 59.38) * mm, "radius": 1.5 * mm});
            skCircle(sketch, "E8.28.9", {"center": v(28.47, 63.95) * mm, "radius": 1.5 * mm});
            skCircle(sketch, "E8.28.10", {"center": v(30.5, 68.52) * mm, "radius": 1.5 * mm});
            skCircle(sketch, "E8.29.0", {"center": v(10.4, 48.9) * mm, "radius": 1.5 * mm});
            skCircle(sketch, "E8.29.1", {"center": v(5.2, 24.45) * mm, "radius": 1.5 * mm});
            skCircle(sketch, "E8.29.2", {"center": v(6.24, 29.34) * mm, "radius": 1.5 * mm});
            skCircle(sketch, "E8.29.3", {"center": v(7.28, 34.24) * mm, "radius": 1.5 * mm});
            skCircle(sketch, "E8.29.4", {"center": v(8.32, 39.13) * mm, "radius": 1.5 * mm});
            skCircle(sketch, "E8.29.5", {"center": v(9.36, 44.02) * mm, "radius": 1.5 * mm});
            skCircle(sketch, "E8.29.6", {"center": v(11.44, 53.8) * mm, "radius": 1.5 * mm});
            skCircle(sketch, "E8.29.7", {"center": v(12.47, 58.69) * mm, "radius": 1.5 * mm});
            skCircle(sketch, "E8.29.8", {"center": v(13.51, 63.58) * mm, "radius": 1.5 * mm});
            skCircle(sketch, "E8.29.9", {"center": v(14.55, 68.47) * mm, "radius": 1.5 * mm});
            skCircle(sketch, "E8.29.10", {"center": v(15.6, 73.36) * mm, "radius": 1.5 * mm});
            skPoint(sketch, "E8.center", {"position": v(0, 0) * mm});
            skSolve(sketch);
        }
        {
            var Q0;
            Q0 = qSketchRegion(id + "F8", true);
            extrude(context, id + "F9", {"entities" : qUnion([Q0]), "operationType" : NewBodyOperationType.REMOVE, "endBound" : BoundingType.UP_TO_NEXT, "oppositeDirection" : true, "depth" : 25 * mm, "offsetDistance" : 25 * mm});
        }
    });
